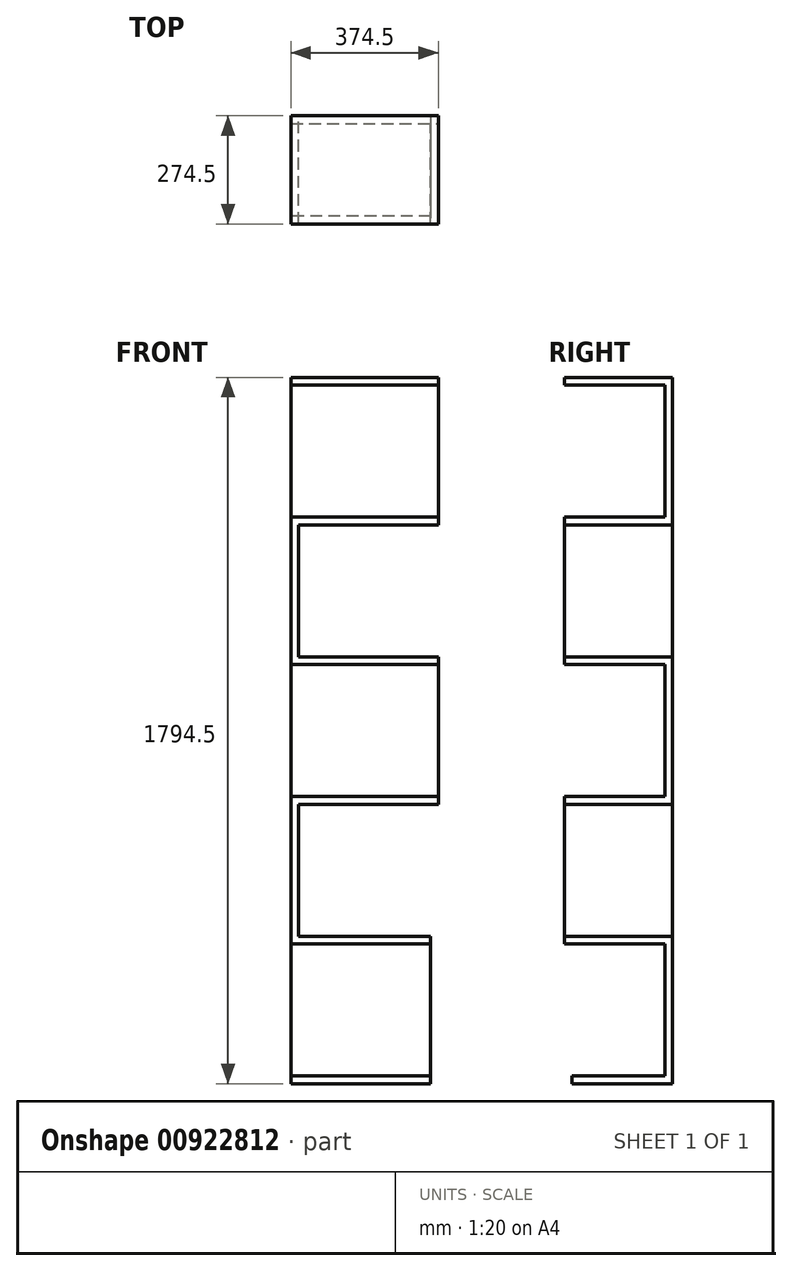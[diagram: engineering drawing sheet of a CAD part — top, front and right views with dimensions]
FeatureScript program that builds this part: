
annotation { "Feature Type Name" : "Feature", "Feature Type Description" : "" }
export const myFeature = defineFeature(function(context is Context, id is Id, definition is map)
    precondition{}
    {
        {
            var Q0;
            Q0=qCreatedBy(makeId("Top.planeOp"),FACE);
            var sketch = newSketch(context, id + "F0", { "sketchPlane" : qUnion([Q0])});
            skLineSegment(sketch, "E0.bottom", {"start": v(177.5, 127.5) * mm, "end": v(-177.5, 127.5) * mm});
            skLineSegment(sketch, "E0.top", {"start": v(177.5, -127.5) * mm, "end": v(-177.5, -127.5) * mm});
            skLineSegment(sketch, "E0.left", {"start": v(177.5, 127.5) * mm, "end": v(177.5, -127.5) * mm});
            skLineSegment(sketch, "E0.right", {"start": v(-177.5, 127.5) * mm, "end": v(-177.5, -127.5) * mm});
            skPoint(sketch, "E0.middle", {"position": v(0, 0) * mm});
            skSolve(sketch);
        }
        {
            var Q0;
            Q0 = qSketchRegion(id + "F0", true);
            extrude(context, id + "F1", {"entities" : qUnion([Q0]), "depth" : 19.5 * mm, "offsetDistance" : 25 * mm});
        }
        {
            var Q0;
            Q0=makeQuery(id+"F1.opExtrude","CAP_FACE",FACE,{"disambiguationData":[OSD([sQuery(id+"F0.wireOp",EDGE,"E0.bottom"),sQuery(id+"F0.wireOp",EDGE,"E0.top"),sQuery(id+"F0.wireOp",EDGE,"E0.left"),sQuery(id+"F0.wireOp",EDGE,"E0.right")])],"isStart":false});
            var sketch = newSketch(context, id + "F2", { "sketchPlane" : qUnion([Q0])});
            skLineSegment(sketch, "E1.bottom", {"start": v(-177.5, 127.5) * mm, "end": v(177.5, 127.5) * mm});
            skLineSegment(sketch, "E1.top", {"start": v(-177.5, 108) * mm, "end": v(177.5, 108) * mm});
            skLineSegment(sketch, "E1.left", {"start": v(-177.5, 127.5) * mm, "end": v(-177.5, 108) * mm});
            skLineSegment(sketch, "E1.right", {"start": v(177.5, 127.5) * mm, "end": v(177.5, 108) * mm});
            skSolve(sketch);
        }
        {
            var Q0;
            Q0 = qSketchRegion(id + "F2", true);
            extrude(context, id + "F3", {"entities" : qUnion([Q0]), "operationType" : NewBodyOperationType.ADD, "depth" : 355 * mm, "offsetDistance" : 25 * mm});
        }
        {
            var Q0;
            Q0=makeQuery(id+"F3.opExtrude","SWEPT_FACE",FACE,{"disambiguationData":[OSD([sQuery(id+"F2.wireOp",EDGE,"E1.top")])]});
            var sketch = newSketch(context, id + "F4", { "sketchPlane" : qUnion([Q0])});
            skLineSegment(sketch, "E2.bottom", {"start": v(-177.5, 374.5) * mm, "end": v(177.5, 374.5) * mm});
            skLineSegment(sketch, "E2.top", {"start": v(-177.5, 355) * mm, "end": v(177.5, 355) * mm});
            skLineSegment(sketch, "E2.left", {"start": v(-177.5, 374.5) * mm, "end": v(-177.5, 355) * mm});
            skLineSegment(sketch, "E2.right", {"start": v(177.5, 374.5) * mm, "end": v(177.5, 355) * mm});
            skSolve(sketch);
        }
        {
            var Q0;
            Q0 = qSketchRegion(id + "F4", true);
            extrude(context, id + "F5", {"entities" : qUnion([Q0]), "operationType" : NewBodyOperationType.ADD, "depth" : 255 * mm, "offsetDistance" : 25 * mm});
        }
        {
            var Q0;
            Q0=makeQuery(id+"F5.boolean.opBoolean","MERGE",FACE,{"derivedFrom":[makeQuery(id+"F3.opExtrude","CAP_FACE",FACE,{"disambiguationData":[OSD([sQuery(id+"F2.wireOp",EDGE,"E1.bottom"),sQuery(id+"F2.wireOp",EDGE,"E1.top"),sQuery(id+"F2.wireOp",EDGE,"E1.left"),sQuery(id+"F2.wireOp",EDGE,"E1.right")])],"isStart":false}),makeQuery(id+"F5.opExtrude","SWEPT_FACE",FACE,{"disambiguationData":[OSD([sQuery(id+"F4.wireOp",EDGE,"E2.bottom")])]})]});
            var sketch = newSketch(context, id + "F6", { "sketchPlane" : qUnion([Q0])});
            skLineSegment(sketch, "E3.bottom", {"start": v(-177.5, -147) * mm, "end": v(-158, -147) * mm});
            skLineSegment(sketch, "E3.top", {"start": v(-177.5, 127.5) * mm, "end": v(-158, 127.5) * mm});
            skLineSegment(sketch, "E3.left", {"start": v(-177.5, -147) * mm, "end": v(-177.5, 127.5) * mm});
            skLineSegment(sketch, "E3.right", {"start": v(-158, -147) * mm, "end": v(-158, 127.5) * mm});
            skSolve(sketch);
        }
        {
            var Q0;
            Q0 = qSketchRegion(id + "F6", true);
            extrude(context, id + "F7", {"entities" : qUnion([Q0]), "operationType" : NewBodyOperationType.ADD, "depth" : 355 * mm, "offsetDistance" : 25 * mm});
        }
        {
            var Q0;
            Q0=makeQuery(id+"F7.opExtrude","SWEPT_FACE",FACE,{"disambiguationData":[OSD([sQuery(id+"F6.wireOp",EDGE,"E3.right")])]});
            var sketch = newSketch(context, id + "F8", { "sketchPlane" : qUnion([Q0])});
            skLineSegment(sketch, "E4.bottom", {"start": v(-147, 729.5) * mm, "end": v(127.5, 729.5) * mm});
            skLineSegment(sketch, "E4.top", {"start": v(-147, 710) * mm, "end": v(127.5, 710) * mm});
            skLineSegment(sketch, "E4.left", {"start": v(-147, 729.5) * mm, "end": v(-147, 710) * mm});
            skLineSegment(sketch, "E4.right", {"start": v(127.5, 729.5) * mm, "end": v(127.5, 710) * mm});
            skSolve(sketch);
        }
        {
            var Q0;
            Q0 = qSketchRegion(id + "F8", true);
            extrude(context, id + "F9", {"entities" : qUnion([Q0]), "operationType" : NewBodyOperationType.ADD, "depth" : 355 * mm, "offsetDistance" : 25 * mm});
        }
        {
            var Q0;
            Q0=makeQuery(id+"F9.boolean.opBoolean","MERGE",FACE,{"derivedFrom":[makeQuery(id+"F7.opExtrude","CAP_FACE",FACE,{"disambiguationData":[OSD([sQuery(id+"F6.wireOp",EDGE,"E3.bottom"),sQuery(id+"F6.wireOp",EDGE,"E3.top"),sQuery(id+"F6.wireOp",EDGE,"E3.left"),sQuery(id+"F6.wireOp",EDGE,"E3.right")])],"isStart":false}),makeQuery(id+"F9.opExtrude","SWEPT_FACE",FACE,{"disambiguationData":[OSD([sQuery(id+"F8.wireOp",EDGE,"E4.bottom")])]})]});
            var sketch = newSketch(context, id + "F10", { "sketchPlane" : qUnion([Q0])});
            skLineSegment(sketch, "E5.bottom", {"start": v(-177.5, 127.5) * mm, "end": v(197, 127.5) * mm});
            skLineSegment(sketch, "E5.top", {"start": v(-177.5, 108) * mm, "end": v(197, 108) * mm});
            skLineSegment(sketch, "E5.left", {"start": v(-177.5, 127.5) * mm, "end": v(-177.5, 108) * mm});
            skLineSegment(sketch, "E5.right", {"start": v(197, 127.5) * mm, "end": v(197, 108) * mm});
            skSolve(sketch);
        }
        {
            var Q0;
            Q0 = qSketchRegion(id + "F10", true);
            extrude(context, id + "F11", {"entities" : qUnion([Q0]), "operationType" : NewBodyOperationType.ADD, "depth" : 355 * mm, "offsetDistance" : 25 * mm});
        }
        {
            var Q0;
            Q0=makeQuery(id+"F11.opExtrude","SWEPT_FACE",FACE,{"disambiguationData":[OSD([sQuery(id+"F10.wireOp",EDGE,"E5.top")])]});
            var sketch = newSketch(context, id + "F12", { "sketchPlane" : qUnion([Q0])});
            skLineSegment(sketch, "E6.bottom", {"start": v(-177.5, 1084.5) * mm, "end": v(197, 1084.5) * mm});
            skLineSegment(sketch, "E6.top", {"start": v(-177.5, 1065) * mm, "end": v(197, 1065) * mm});
            skLineSegment(sketch, "E6.left", {"start": v(-177.5, 1084.5) * mm, "end": v(-177.5, 1065) * mm});
            skLineSegment(sketch, "E6.right", {"start": v(197, 1084.5) * mm, "end": v(197, 1065) * mm});
            skSolve(sketch);
        }
        {
            var Q0;
            Q0 = qSketchRegion(id + "F12", true);
            extrude(context, id + "F13", {"entities" : qUnion([Q0]), "operationType" : NewBodyOperationType.ADD, "depth" : 255 * mm, "offsetDistance" : 25 * mm});
        }
        {
            var Q0;
            Q0=makeQuery(id+"F13.boolean.opBoolean","MERGE",FACE,{"derivedFrom":[makeQuery(id+"F11.opExtrude","CAP_FACE",FACE,{"disambiguationData":[OSD([sQuery(id+"F10.wireOp",EDGE,"E5.bottom"),sQuery(id+"F10.wireOp",EDGE,"E5.top"),sQuery(id+"F10.wireOp",EDGE,"E5.left"),sQuery(id+"F10.wireOp",EDGE,"E5.right")])],"isStart":false}),makeQuery(id+"F13.opExtrude","SWEPT_FACE",FACE,{"disambiguationData":[OSD([sQuery(id+"F12.wireOp",EDGE,"E6.bottom")])]})]});
            var sketch = newSketch(context, id + "F14", { "sketchPlane" : qUnion([Q0])});
            skLineSegment(sketch, "E7.bottom", {"start": v(-177.5, -147) * mm, "end": v(-158, -147) * mm});
            skLineSegment(sketch, "E7.top", {"start": v(-177.5, 127.5) * mm, "end": v(-158, 127.5) * mm});
            skLineSegment(sketch, "E7.left", {"start": v(-177.5, -147) * mm, "end": v(-177.5, 127.5) * mm});
            skLineSegment(sketch, "E7.right", {"start": v(-158, -147) * mm, "end": v(-158, 127.5) * mm});
            skSolve(sketch);
        }
        {
            var Q0;
            Q0 = qSketchRegion(id + "F14", true);
            extrude(context, id + "F15", {"entities" : qUnion([Q0]), "operationType" : NewBodyOperationType.ADD, "depth" : 355 * mm, "offsetDistance" : 25 * mm});
        }
        {
            var Q0;
            Q0=makeQuery(id+"F15.opExtrude","SWEPT_FACE",FACE,{"disambiguationData":[OSD([sQuery(id+"F14.wireOp",EDGE,"E7.right")])]});
            var sketch = newSketch(context, id + "F16", { "sketchPlane" : qUnion([Q0])});
            skLineSegment(sketch, "E8.bottom", {"start": v(-147, 1439.5) * mm, "end": v(127.5, 1439.5) * mm});
            skLineSegment(sketch, "E8.top", {"start": v(-147, 1420) * mm, "end": v(127.5, 1420) * mm});
            skLineSegment(sketch, "E8.left", {"start": v(-147, 1439.5) * mm, "end": v(-147, 1420) * mm});
            skLineSegment(sketch, "E8.right", {"start": v(127.5, 1439.5) * mm, "end": v(127.5, 1420) * mm});
            skSolve(sketch);
        }
        {
            var Q0;
            Q0 = qSketchRegion(id + "F16", true);
            extrude(context, id + "F17", {"entities" : qUnion([Q0]), "operationType" : NewBodyOperationType.ADD, "depth" : 355 * mm, "offsetDistance" : 25 * mm});
        }
        {
            var Q0;
            Q0=makeQuery(id+"F17.boolean.opBoolean","MERGE",FACE,{"derivedFrom":[makeQuery(id+"F15.opExtrude","CAP_FACE",FACE,{"disambiguationData":[OSD([sQuery(id+"F14.wireOp",EDGE,"E7.bottom"),sQuery(id+"F14.wireOp",EDGE,"E7.top"),sQuery(id+"F14.wireOp",EDGE,"E7.left"),sQuery(id+"F14.wireOp",EDGE,"E7.right")])],"isStart":false}),makeQuery(id+"F17.opExtrude","SWEPT_FACE",FACE,{"disambiguationData":[OSD([sQuery(id+"F16.wireOp",EDGE,"E8.bottom")])]})]});
            var sketch = newSketch(context, id + "F18", { "sketchPlane" : qUnion([Q0])});
            skLineSegment(sketch, "E9.bottom", {"start": v(-177.5, 127.5) * mm, "end": v(197, 127.5) * mm});
            skLineSegment(sketch, "E9.top", {"start": v(-177.5, 108) * mm, "end": v(197, 108) * mm});
            skLineSegment(sketch, "E9.left", {"start": v(-177.5, 127.5) * mm, "end": v(-177.5, 108) * mm});
            skLineSegment(sketch, "E9.right", {"start": v(197, 127.5) * mm, "end": v(197, 108) * mm});
            skSolve(sketch);
        }
        {
            var Q0;
            Q0 = qSketchRegion(id + "F18", true);
            extrude(context, id + "F19", {"entities" : qUnion([Q0]), "operationType" : NewBodyOperationType.ADD, "depth" : 355 * mm, "offsetDistance" : 25 * mm});
        }
        {
            var Q0;
            Q0=makeQuery(id+"F19.opExtrude","SWEPT_FACE",FACE,{"disambiguationData":[OSD([sQuery(id+"F18.wireOp",EDGE,"E9.top")])]});
            var sketch = newSketch(context, id + "F20", { "sketchPlane" : qUnion([Q0])});
            skLineSegment(sketch, "E10.bottom", {"start": v(197, 1794.5) * mm, "end": v(-177.5, 1794.5) * mm});
            skLineSegment(sketch, "E10.top", {"start": v(197, 1775) * mm, "end": v(-177.5, 1775) * mm});
            skLineSegment(sketch, "E10.left", {"start": v(197, 1794.5) * mm, "end": v(197, 1775) * mm});
            skLineSegment(sketch, "E10.right", {"start": v(-177.5, 1794.5) * mm, "end": v(-177.5, 1775) * mm});
            skSolve(sketch);
        }
        {
            var Q0;
            Q0 = qSketchRegion(id + "F20", true);
            extrude(context, id + "F21", {"entities" : qUnion([Q0]), "operationType" : NewBodyOperationType.ADD, "depth" : 255 * mm, "offsetDistance" : 25 * mm});
        }
    });
